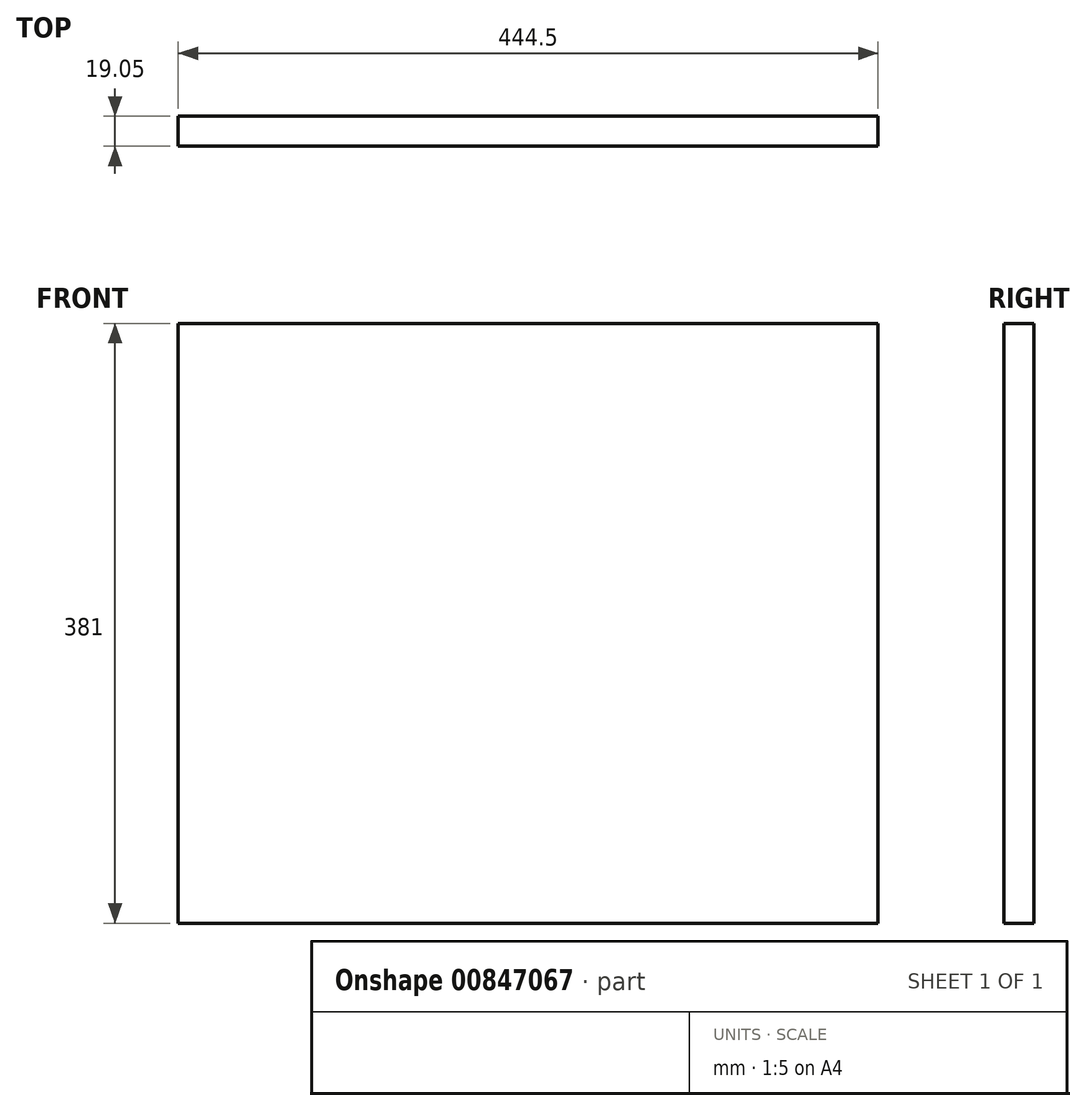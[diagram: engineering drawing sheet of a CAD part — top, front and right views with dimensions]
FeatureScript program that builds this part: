
annotation { "Feature Type Name" : "Feature", "Feature Type Description" : "" }
export const myFeature = defineFeature(function(context is Context, id is Id, definition is map)
    precondition{}
    {
        {
            var Q0;
            Q0=qCreatedBy(makeId("Front.planeOp"),FACE);
            var sketch = newSketch(context, id + "F0", { "sketchPlane" : qUnion([Q0])});
            skLineSegment(sketch, "E0.bottom", {"start": v(-222.25, 228.6) * mm, "end": v(222.25, 228.6) * mm});
            skLineSegment(sketch, "E0.top", {"start": v(-222.25, -152.4) * mm, "end": v(222.25, -152.4) * mm});
            skLineSegment(sketch, "E0.left", {"start": v(-222.25, 228.6) * mm, "end": v(-222.25, -152.4) * mm});
            skLineSegment(sketch, "E0.right", {"start": v(222.25, 228.6) * mm, "end": v(222.25, -152.4) * mm});
            skSolve(sketch);
        }
        {
            var Q0;
            Q0=makeQuery(id+"F0.imprint","IMPRINT",FACE,{"disambiguationData":[TD([[makeQuery(id+"F0.imprint","IMPRINT",EDGE,{"derivedFrom":sQuery(id+"F0.wireOp",EDGE,"E0.bottom")}),-1.0]])]});
            extrude(context, id + "F1", {"entities" : qUnion([Q0]), "depth" : 19.05 * mm, "offsetDistance" : 25.4 * mm});
        }
    });
